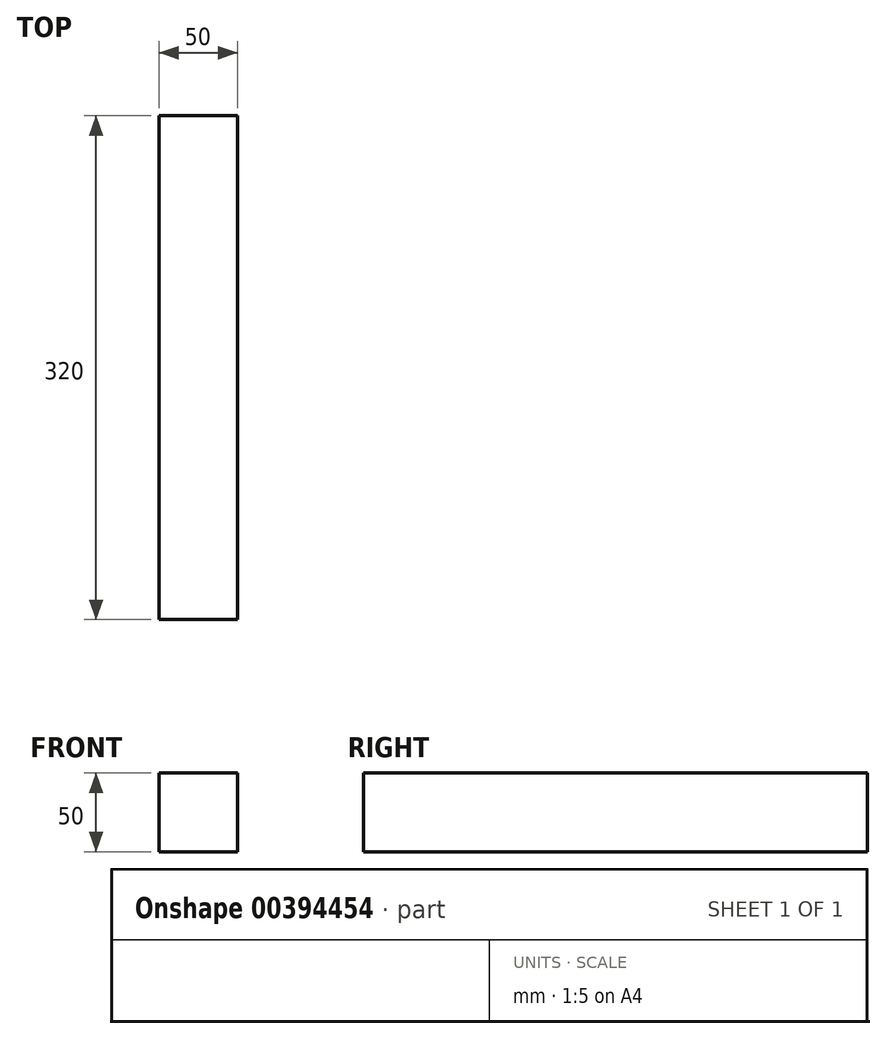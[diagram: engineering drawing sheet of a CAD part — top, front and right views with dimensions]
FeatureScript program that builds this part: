
annotation { "Feature Type Name" : "Feature", "Feature Type Description" : "" }
export const myFeature = defineFeature(function(context is Context, id is Id, definition is map)
    precondition{}
    {
        {
            var Q0;
            Q0=qCreatedBy(makeId("Top.planeOp"),FACE);
            var sketch = newSketch(context, id + "F0", { "sketchPlane" : qUnion([Q0])});
            skLineSegment(sketch, "E0.bottom", {"start": v(25, -160) * mm, "end": v(-25, -160) * mm});
            skLineSegment(sketch, "E0.top", {"start": v(25, 160) * mm, "end": v(-25, 160) * mm});
            skLineSegment(sketch, "E0.left", {"start": v(25, -160) * mm, "end": v(25, 160) * mm});
            skLineSegment(sketch, "E0.right", {"start": v(-25, -160) * mm, "end": v(-25, 160) * mm});
            skPoint(sketch, "E0.middle", {"position": v(0, 0) * mm});
            skSolve(sketch);
        }
        {
            var Q0;
            Q0=makeQuery(id+"F0.imprint","IMPRINT",FACE,{"disambiguationData":[TD([[makeQuery(id+"F0.imprint","IMPRINT",EDGE,{"derivedFrom":sQuery(id+"F0.wireOp",EDGE,"E0.bottom")}),-1.0]])]});
            extrude(context, id + "F1", {"entities" : qUnion([Q0]), "depth" : 50 * mm});
        }
    });
